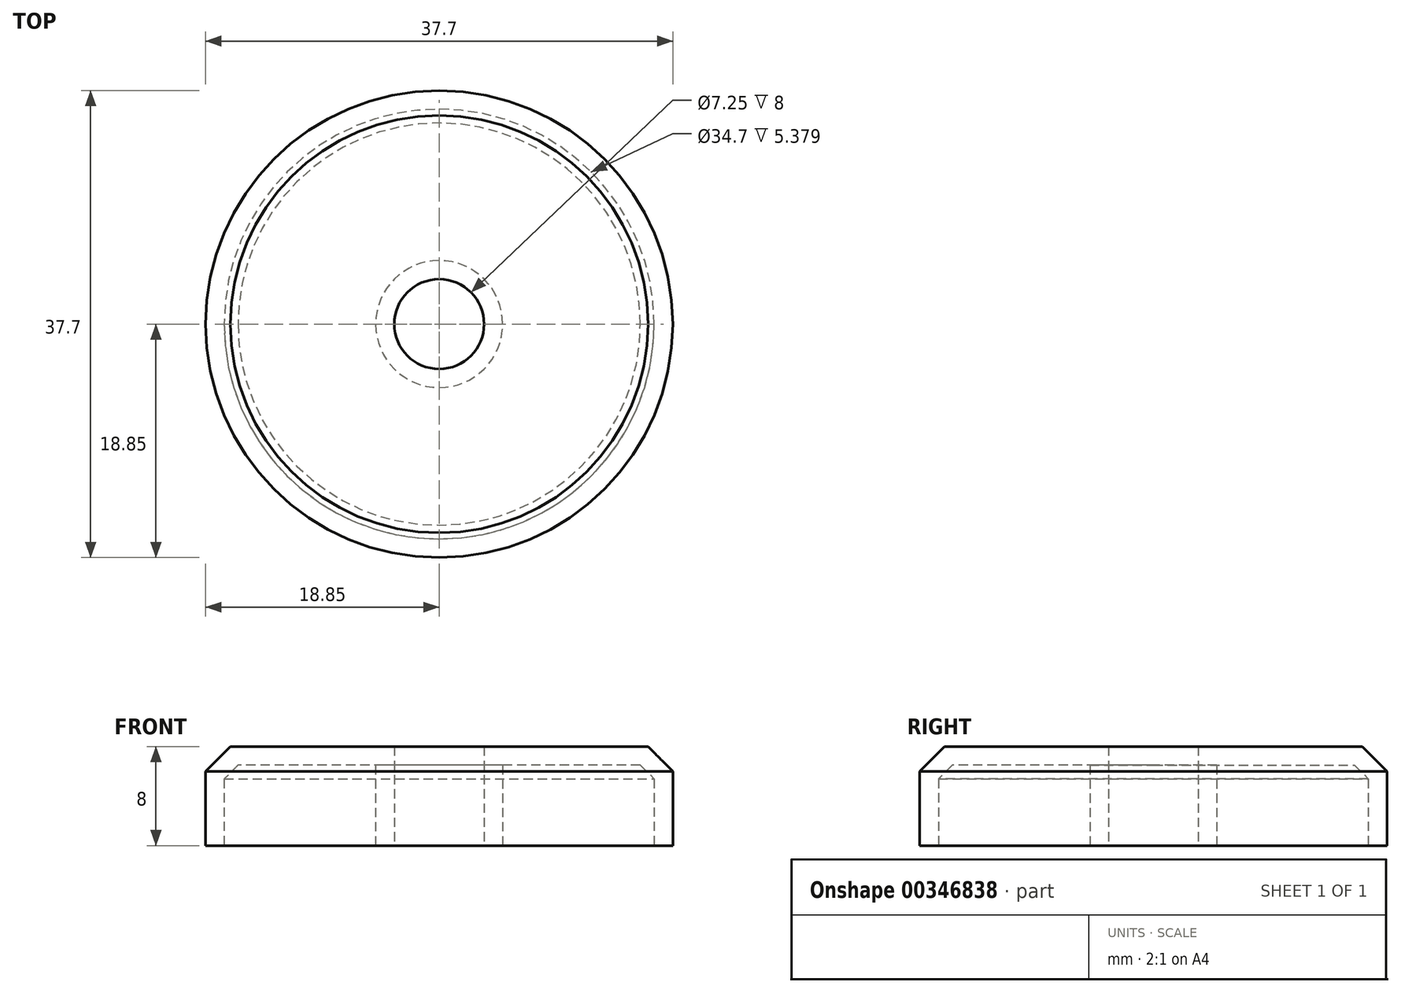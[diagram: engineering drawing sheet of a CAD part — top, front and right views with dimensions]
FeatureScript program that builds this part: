
annotation { "Feature Type Name" : "Feature", "Feature Type Description" : "" }
export const myFeature = defineFeature(function(context is Context, id is Id, definition is map)
    precondition{}
    {
        {
            var Q0;
            Q0=qCreatedBy(makeId("Top.planeOp"),FACE);
            var sketch = newSketch(context, id + "F0", { "sketchPlane" : qUnion([Q0])});
            skCircle(sketch, "E0", {"center": v(0, 0) * mm, "radius": 18.85 * mm});
            skCircle(sketch, "E1", {"center": v(0, 0) * mm, "radius": 3.62 * mm});
            skSolve(sketch);
        }
        {
            var Q0;
            Q0=makeQuery(id+"F0.imprint","IMPRINT",FACE,{"disambiguationData":[TD([[makeQuery(id+"F0.imprint","IMPRINT",EDGE,{"derivedFrom":sQuery(id+"F0.wireOp",EDGE,"E0")}),1.0]])]});
            extrude(context, id + "F1", {"entities" : qUnion([Q0]), "depth" : 8 * mm});
        }
        {
            var Q0;
            Q0=makeQuery(id+"F1.opExtrude","CAP_EDGE",EDGE,{"disambiguationData":[OSD([sQuery(id+"F0.wireOp",EDGE,"E0")])],"isStart":false});
            chamfer(context, id + "F2", {"entities" : qUnion([Q0]), "width" : 2 * mm, "tangentPropagation" : true});
        }
        {
            var Q0;
            Q0=makeQuery(id+"F1.opExtrude","CAP_FACE",FACE,{"disambiguationData":[OSD([sQuery(id+"F0.wireOp",EDGE,"E0"),sQuery(id+"F0.wireOp",EDGE,"E1")])],"isStart":true});
            shell(context, id + "F3", {"entities" : qUnion([Q0]), "thickness" : 1.5 * mm});
        }
    });
